# Revit family: Shower-Ceiling_Mount-Showerarm-KOHLER-Assembly-K-26326_1
name_source: partatom
category: Plumbing Fixtures
revit_build: Autodesk Revit 2017 (Build: 20160225_1515(x64)
units: mm (PartAtom-declared; Revit-internal decimal feet)

## family parameters
Cut with Voids When Loaded = No
Host = Face
OmniClass Number = 23.31.17.00
OmniClass Title = Showers
Part Type = Normal
Room Calculation Point = No
Round Connector Dimension = Use Diameter
Shared = No

## types (4) — shared parameters
ADA Compliant = No
Assembly Code = D2010700
CW Connection = Yes
Cold Water Inlet = Cold Water Inlet
Date Modified = 12/15/2020
Default Elevation = 0"
Description = 10inch Ceiling Arm
Drain Included = No
Flow Rate = 0 GPM
HW Connection = Yes
Height = 12 3/4"
Hot Water Inlet = Hot Water Inlet
Length = 2 3/4"
Manufacturer = KOHLER Co.
Master Format 2014 = 22 42 23
Master Format 2014 Name = Residential Showers
Material = Brass Construction
Pressure = 0.00 psi
Product Documentation Link = https://www.us.kohler.com
Product Name = Assembly
Product Page URL = http://www.us.kohler.com
URL = https://www.us.kohler.com
Vent Connection = No
Waste Connection = No
Waste Water Outlet = Waste Water Outlet
WaterSense Certified = No
Width = 4 9/16"

## per-type parameters (varying)
| type | Finish | Model | Type |
| CP-Polished Chrome | Kohler-Metal-CP-Polished_Chrome | K-26326-CP | 1 |
| BN-Vibrant Brusshed Nickel | Kohler-Metal-BN-Vibrant_Brushed_Nickel | K-26326-BN | 2 |
| BL-Matte Black | Kohler-Metal-BL-Matte_Black | K-26326-BL | 3 |
| 2MB-Vibrant Moderne Brushed Brass | Kohler-Metal-2MB-Vibrant_Brushed_Moderne_Brass | K-26326-2MB | 4 |

## geometry (parser evidence)
native form markers: Sweep x5
no freeform markers — native parametric forms only
